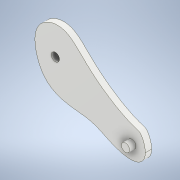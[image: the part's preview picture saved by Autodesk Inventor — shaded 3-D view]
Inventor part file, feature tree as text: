
AUTODESK INVENTOR PART (.ipt)
format: ipt  version: 2022 (Build 260153000, 153)  size: 129,024 bytes
history: native  units: in
note: dims shown in document units (in); Inventor stores cm internally (conversion verified against a paired STEP export)
features: extrude x2, sketch x1
ambient origin geometry x8: Origin, YZ Plane, XZ Plane, XY Plane, X Axis, Y Axis, Z Axis, Center Point
bodies: Solid1 (feature_tree)
feature tree (3):
  sketch  "Sketch2"  dims[d0=0.1969in d1=0.0in d2=0.1969in d3=0.0in d4=0.2559in]
  extrude  "Extrusion1"  TaperAngle=0.0deg  [1 undecoded]
  extrude  "Extrusion2"  Depth=0.1969in TaperAngle=0.0deg
note: 1 required parameter value undecoded (feature->parameter linkage not recoverable at this tier; creation-order binding heuristic only, values carry confidence <= 0.55)
